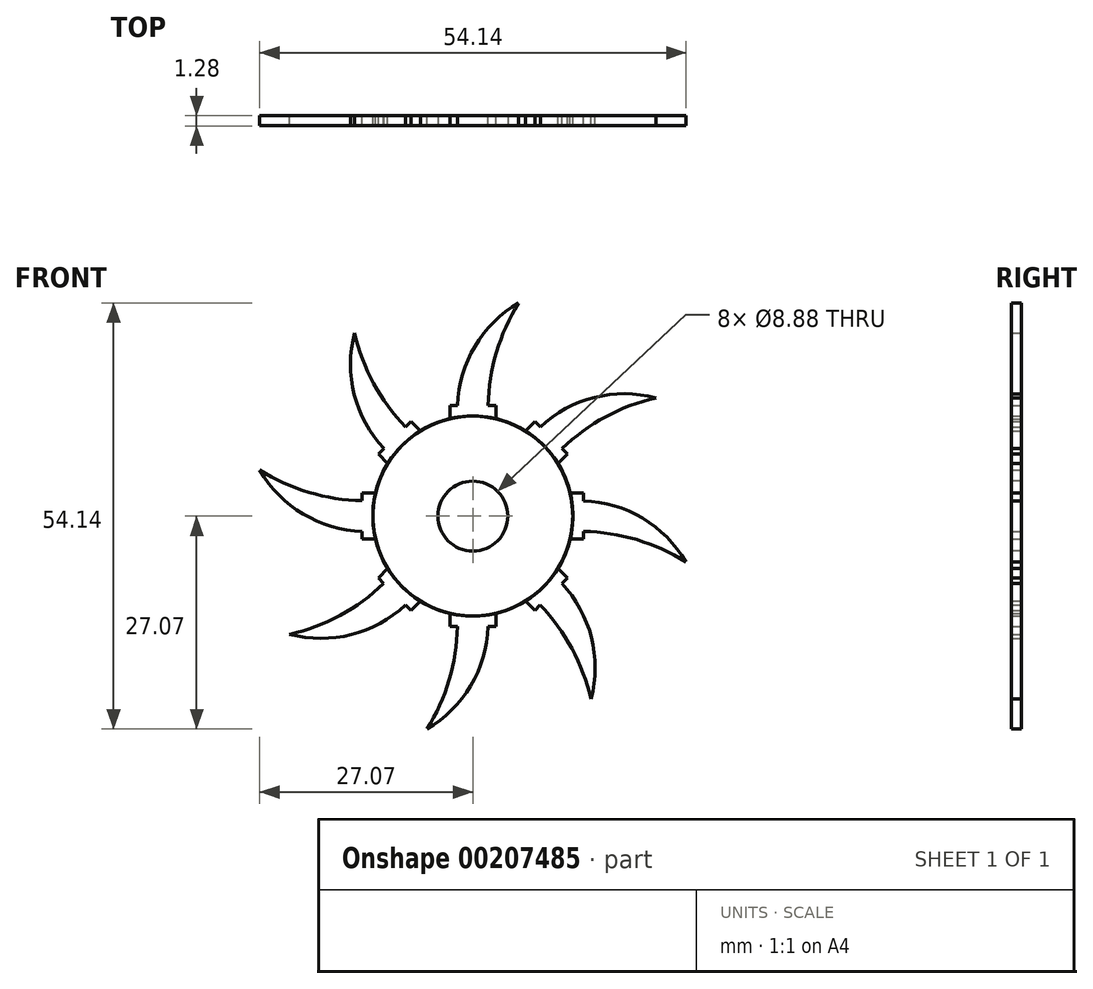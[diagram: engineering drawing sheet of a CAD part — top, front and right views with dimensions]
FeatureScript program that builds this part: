
annotation { "Feature Type Name" : "Feature", "Feature Type Description" : "" }
export const myFeature = defineFeature(function(context is Context, id is Id, definition is map)
    precondition{}
    {
        {
            var Q0;
            Q0=qCreatedBy(makeId("Front.planeOp"),FACE);
            var sketch = newSketch(context, id + "F0", { "sketchPlane" : qUnion([Q0])});
            skCircle(sketch, "E0", {"center": v(0, 0) * mm, "radius": 12.7 * mm});
            skSolve(sketch);
        }
        {
            var Q0;
            Q0=qSketchRegion(id+"F0",true);
            extrude(context, id + "F1", {"entities" : qUnion([Q0]), "endBound" : BoundingType.SYMMETRIC, "depth" : 1.27 * mm});
        }
        {
            var Q0;
            Q0=qCreatedBy(makeId("Front.planeOp"),FACE);
            var sketch = newSketch(context, id + "F2", { "sketchPlane" : qUnion([Q0])});
            skPoint(sketch, "E1.middle", {"position": v(0, 12.38) * mm});
            skArc(sketch, "E2", {"start": v(5.83, 27.07) * mm, "mid": v(0.14, 21.34) * mm, "end": v(-1.94, 13.55) * mm});
            skArc(sketch, "E3", {"start": v(5.83, 27.07) * mm, "mid": v(2.93, 20.58) * mm, "end": v(1.94, 13.55) * mm});
            skLineSegment(sketch, "E4.bottom", {"start": v(2.93, 10.7) * mm, "end": v(-2.93, 10.7) * mm});
            skLineSegment(sketch, "E4.top", {"start": v(2.93, 14.05) * mm, "end": v(-2.93, 14.05) * mm});
            skLineSegment(sketch, "E4.left", {"start": v(2.93, 10.7) * mm, "end": v(2.93, 14.05) * mm});
            skLineSegment(sketch, "E4.right", {"start": v(-2.93, 10.7) * mm, "end": v(-2.93, 14.05) * mm});
            skSolve(sketch);
        }
        {
            var Q0;
            Q0=qSketchRegion(id+"F2",true);
            extrude(context, id + "F3", {"entities" : qUnion([Q0]), "operationType" : NewBodyOperationType.ADD, "endBound" : BoundingType.SYMMETRIC, "depth" : 1.27 * mm});
        }
        {
            var Q0;
            Q0=makeQuery(id+"F1.opExtrude","SWEPT_BODY",BODY,{"disambiguationData":[OSD([sQuery(id+"F0.wireOp",EDGE,"E0")])]});
            var Q1;
            Q1=sQuery(id+"F0.wireOp",EDGE,"E0");
            circularPattern(context, id + "F4", {"entities" : qUnion([Q0]), "axis" : qUnion([Q1]), "angle" : 360 * degree, "instanceCount" : 8, "equalSpace" : true});
        }
        {
            var Q0;
            Q0=qCreatedBy(makeId("Front.planeOp"),FACE);
            var sketch = newSketch(context, id + "F5", { "sketchPlane" : qUnion([Q0])});
            skCircle(sketch, "E5", {"center": v(0, 0) * mm, "radius": 4.44 * mm});
            skSolve(sketch);
        }
        {
            var Q0;
            Q0=qSketchRegion(id+"F5",true);
            extrude(context, id + "F6", {"entities" : qUnion([Q0]), "operationType" : NewBodyOperationType.REMOVE, "endBound" : BoundingType.SYMMETRIC, "oppositeDirection" : true, "depth" : 1.27 * mm});
        }
    });
